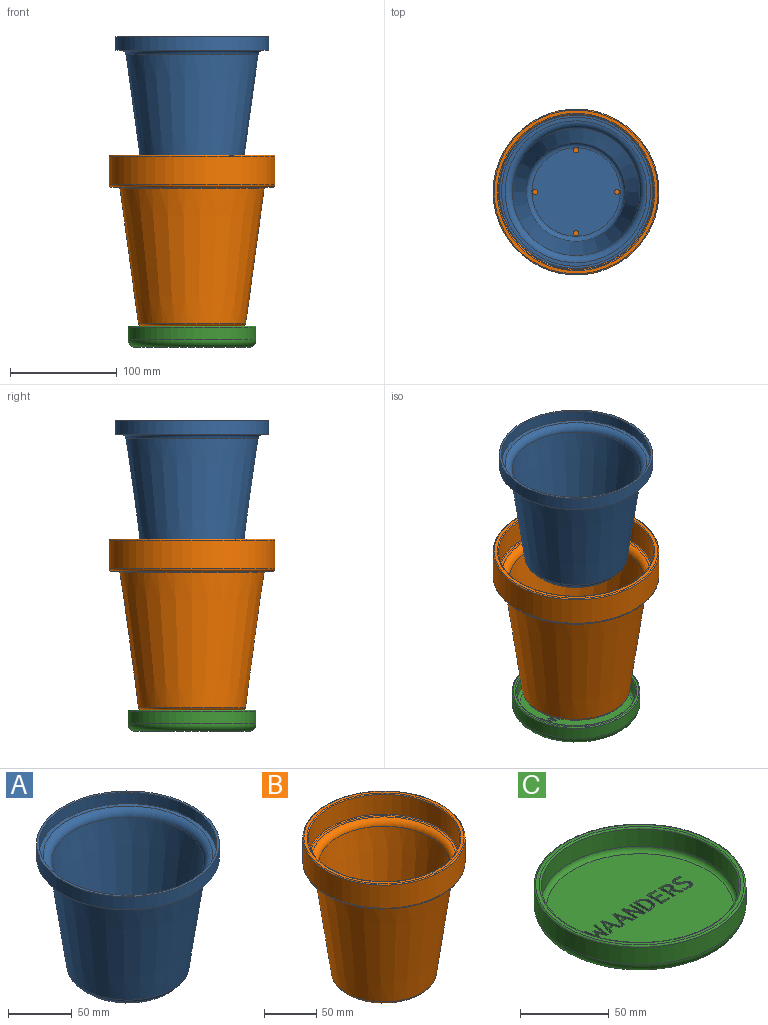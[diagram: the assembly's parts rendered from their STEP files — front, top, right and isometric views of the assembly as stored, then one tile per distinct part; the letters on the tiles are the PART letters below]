
ASSEMBLY  parts=3 mates=2
PART A: 18 faces, bbox 152.3x152.3x122.5 mm
  f0: plane 143.69x143.69mm, normal (0,0,1), area 890.3mm2, adj f1,f11
  f1: cylinder r=69.84mm len=139.69mm, axis (0,0,-1), area 4718.3mm2, adj f0,f2
  f2: cone r=66.5mm half-angle=89.8deg, axis (0,0,1), area 1430.4mm2, adj f1,f3
  f3: torus R=66.8mm, axis (0,0,-1), area 3821.9mm2, adj f2,f4
  f4: cone r=46.37mm half-angle=7.9deg, axis (0,0,1), area 32806.2mm2, adj f3,f5
  f5: torus R=41.42mm, axis (0,0,-1), area 2000.3mm2, adj f4,f6,f12
  f6: plane 82.84x82.84mm, normal (0,0,1), area 5311.8mm2, adj f5,f12,f13,f14,f15
  f7: torus R=43.16mm, axis (0,0,-1), area 2078.9mm2, adj f8,f16
  f8: cone r=48.12mm half-angle=7.9deg, axis (0,0,1), area 34557.6mm2, adj f7,f9
  f9: torus R=66.8mm, axis (0,0,-1), area 2871.9mm2, adj f8,f10
  f10: plane 143.69x143.69mm, normal (0,0,-1), area 2197.8mm2, adj f9,f11
  f11: cylinder r=71.84mm len=143.69mm, axis (0,0,-1), area 5758.6mm2, adj f0,f10
  f12: cylinder r=2.5mm len=5mm, axis (0,0,-1), area 62.8mm2, adj f5,f6,f17
  f13: cylinder r=2.5mm len=5mm, axis (0,0,-1), area 62.8mm2, adj f6,f17
  f14: cylinder r=2.5mm len=5mm, axis (0,0,-1), area 62.8mm2, adj f6,f17
  f15: cylinder r=2.5mm len=5mm, axis (0,0,-1), area 62.8mm2, adj f6,f17
  f16: cylinder r=43.16mm len=86.33mm, axis (0,0,1), area 542.4mm2, adj f7,f17
  f17: plane 86.33x86.33mm, normal (0,0,-1), area 5774.6mm2, adj f12,f13,f14,f15,f16
PART B: 150 faces, bbox 168.2x168.2x160 mm
  f0: plane 94.76x94.76mm, normal (0,0,-1), area 6749.7mm2, adj f15,f21,f22,f23,f24,f25,f26,f27
  f1: torus R=69.47mm, axis (0,0,-1), area 1231.2mm2, adj f2,f16
  f2: plane 151.44x151.44mm, normal (0,0,-1), area 2852.6mm2, adj f1,f3
  f3: torus R=75.72mm, axis (0,0,-1), area 1519.8mm2, adj f2,f4
  f4: cylinder r=77.72mm len=155.44mm, axis (0,0,-1), area 13186.1mm2, adj f3,f5
  f5: torus R=76.72mm, axis (0,0,-1), area 762.4mm2, adj f4,f6
  f6: cone r=76.72mm half-angle=89.9deg, axis (0,0,-1), area 1417.9mm2, adj f5,f7
  f7: torus R=73.72mm, axis (0,0,-1), area 722.4mm2, adj f6,f8
  f8: cylinder r=72.72mm len=145.44mm, axis (0,0,-1), area 10513.3mm2, adj f7,f9
  f9: torus R=71.72mm, axis (0,0,-1), area 714.1mm2, adj f8,f10
  f10: plane 143.44x143.44mm, normal (0,0,1), area 999.8mm2, adj f9,f11
  f11: torus R=69.47mm, axis (0,0,-1), area 4119mm2, adj f10,f12
  f12: cone r=45.99mm half-angle=7.8deg, axis (0,0,1), area 41754.1mm2, adj f11,f13
  f13: torus R=43.02mm, axis (0,0,-1), area 1212.7mm2, adj f12,f14
  f14: plane 86.03x86.03mm, normal (0,0,1), area 5813.3mm2, adj f13
  f15: torus R=47.38mm, axis (0,0,-1), area 1330.8mm2, adj f0,f16
  f16: cone r=50.35mm half-angle=7.8deg, axis (0,0,1), area 46955.4mm2, adj f1,f15
  f17: plane 2.97x2mm, normal (0.95,-0.3,0), area 6.2mm2, adj f18,f29,f30,f146
  f18: plane 2.7x2mm, normal (0,1,0), area 5.4mm2, adj f17,f19,f30,f146
  f19: plane 3.27x2mm, normal (-0.96,-0.29,0), area 6.8mm2, adj f18,f20,f30,f146
  f20: extruded ~2x1.28mm, area 2.6mm2, adj f19,f29,f30,f146
  f21: plane 3.17x2mm, normal (0.95,-0.3,0), area 6.7mm2, adj f0,f22,f28,f30
  f22: plane 2x1.34mm, normal (0,-1,0), area 2.7mm2, adj f0,f21,f23,f30
  f23: plane 10.28x3.4mm, normal (-0.95,0.31,0), area 21.7mm2, adj f0,f22,f24,f30
  f24: plane 2x1.36mm, normal (0,1,0), area 2.7mm2, adj f0,f23,f25,f30
  f25: plane 10.28x3.38mm, normal (0.95,0.31,0), area 21.6mm2, adj f0,f24,f26,f30
  f26: plane 2x1.33mm, normal (0,-1,0), area 2.7mm2, adj f0,f25,f27,f30
  f27: plane 3.17x2mm, normal (-0.95,-0.31,0), area 6.7mm2, adj f0,f26,f28,f30
  f28: plane 3.44x2mm, normal (0,-1,0), area 6.9mm2, adj f0,f21,f27,f30
  f29: extruded ~2x1.58mm, area 3.3mm2, adj f17,f20,f30,f146
  f30: plane 10.28x8.14mm, normal (0,0,-1), area 28.9mm2, adj f17,f18,f19,f20,f21,f22,f23,f24
  f31: plane 2x1.25mm, normal (1,0,0), area 2.5mm2, adj f0,f32,f50,f51
  f32: extruded ~2.9x2mm, area 5.9mm2, adj f0,f31,f33,f51
  f33: extruded ~2.76x2mm, area 5.8mm2, adj f0,f32,f34,f51
  f34: extruded ~2.11x2mm, area 4.8mm2, adj f0,f33,f35,f51
  f35: extruded ~2x1.68mm, area 3.6mm2, adj f0,f34,f36,f51
  f36: extruded ~2.3x2mm, area 5.3mm2, adj f0,f35,f37,f51
  f37: extruded ~2x1.89mm, area 4.2mm2, adj f0,f36,f38,f51
  f38: extruded ~2x1.15mm, area 2.5mm2, adj f0,f37,f39,f51
  f39: extruded ~2.05x2mm, area 5.7mm2, adj f0,f38,f40,f51
  f40: extruded ~2.52x2mm, area 5.2mm2, adj f0,f39,f41,f51
  f41: plane 2x1.15mm, normal (-0.93,-0.36,0), area 2.5mm2, adj f0,f40,f42,f51
  f42: extruded ~2.91x2mm, area 6mm2, adj f0,f41,f43,f51
  f43: extruded ~2.47x2mm, area 5.2mm2, adj f0,f42,f44,f51
  f44: extruded ~2x1.91mm, area 4.4mm2, adj f0,f43,f45,f51
  f45: extruded ~2x1.85mm, area 4mm2, adj f0,f44,f46,f51
  f46: extruded ~2.09x2mm, area 4.9mm2, adj f0,f45,f47,f51
  f47: extruded ~2x2mm, area 4.4mm2, adj f0,f46,f48,f51
  f48: extruded ~2x1.12mm, area 2.5mm2, adj f0,f47,f49,f51
  f49: extruded ~2.45x2mm, area 6.8mm2, adj f0,f48,f50,f51
  f50: extruded ~2.9x2mm, area 6mm2, adj f0,f31,f49,f51
  f51: plane 10.52x6.62mm, normal (0,0,-1), area 26.4mm2, adj f31,f32,f33,f34,f35,f36,f37,f38
  f52: plane 5.89x2mm, normal (0,-1,0), area 11.8mm2, adj f0,f53,f63,f64
  f53: plane 2x1.15mm, normal (-1,0,0), area 2.3mm2, adj f0,f52,f54,f64
  f54: plane 4.59x2mm, normal (0,1,0), area 9.2mm2, adj f0,f53,f55,f64
  f55: plane 3.64x2mm, normal (-1,0,0), area 7.3mm2, adj f0,f54,f56,f64
  f56: plane 4.32x2mm, normal (0,-1,0), area 8.6mm2, adj f0,f55,f57,f64
  f57: plane 2x1.13mm, normal (-1,0,0), area 2.3mm2, adj f0,f56,f58,f64
  f58: plane 4.32x2mm, normal (0,1,0), area 8.6mm2, adj f0,f57,f59,f64
  f59: plane 3.16x2mm, normal (-1,0,0), area 6.3mm2, adj f0,f58,f60,f64
  f60: plane 4.59x2mm, normal (0,-1,0), area 9.2mm2, adj f0,f59,f61,f64
  f61: plane 2x1.15mm, normal (-1,0,0), area 2.3mm2, adj f0,f60,f62,f64
  f62: plane 5.89x2mm, normal (0,1,0), area 11.8mm2, adj f0,f61,f63,f64
  f63: plane 10.24x2mm, normal (1,0,0), area 20.5mm2, adj f0,f52,f62,f64
  f64: plane 10.24x5.89mm, normal (0,0,-1), area 28.8mm2, adj f52,f53,f54,f55,f56,f57,f58,f59
  f65: plane 2x1.51mm, normal (0,-1,0), area 3mm2, adj f0,f66,f78,f79
  f66: plane 10.24x2mm, normal (-1,0,0), area 20.5mm2, adj f0,f65,f67,f79
  f67: plane 2x1.22mm, normal (0,1,0), area 2.4mm2, adj f0,f66,f68,f79
  f68: plane 5.6x2mm, normal (1,0,0), area 11.2mm2, adj f0,f67,f69,f79
  f69: extruded ~2.83x2mm, area 5.7mm2, adj f0,f68,f70,f79
  f70: plane 2x0.04mm, normal (0,1,0), area 0.1mm2, adj f0,f69,f71,f79
  f71: plane 8.43x4.05mm, normal (-0.9,0.43,0), area 18.7mm2, adj f0,f70,f72,f79
  f72: plane 2x1.49mm, normal (0,1,0), area 3mm2, adj f0,f71,f73,f79
  f73: plane 10.24x2mm, normal (1,0,0), area 20.5mm2, adj f0,f72,f74,f79
  f74: plane 2x1.2mm, normal (0,-1,0), area 2.4mm2, adj f0,f73,f75,f79
  f75: plane 5.55x2mm, normal (-1,0,0), area 11.1mm2, adj f0,f74,f76,f79
  f76: extruded ~2.92x2mm, area 5.8mm2, adj f0,f75,f77,f79
  f77: plane 2x0.06mm, normal (0,-1,0), area 0.1mm2, adj f0,f76,f78,f79
  f78: plane 8.47x4.06mm, normal (0.9,-0.43,0), area 18.8mm2, adj f0,f65,f77,f79
  f79: plane 10.24x6.7mm, normal (0,0,-1), area 35.1mm2, adj f65,f66,f67,f68,f69,f70,f71,f72
  f80: plane 2.97x2mm, normal (0.95,-0.3,0), area 6.2mm2, adj f81,f92,f93,f147
  f81: plane 2.7x2mm, normal (0,1,0), area 5.4mm2, adj f80,f82,f93,f147
  f82: plane 3.27x2mm, normal (-0.96,-0.29,0), area 6.8mm2, adj f81,f83,f93,f147
  f83: extruded ~2x1.28mm, area 2.6mm2, adj f82,f92,f93,f147
  f84: plane 3.17x2mm, normal (0.95,-0.3,0), area 6.7mm2, adj f0,f85,f91,f93
  f85: plane 2x1.34mm, normal (0,-1,0), area 2.7mm2, adj f0,f84,f86,f93
  f86: plane 10.28x3.4mm, normal (-0.95,0.31,0), area 21.7mm2, adj f0,f85,f87,f93
  f87: plane 2x1.36mm, normal (0,1,0), area 2.7mm2, adj f0,f86,f88,f93
  f88: plane 10.28x3.38mm, normal (0.95,0.31,0), area 21.6mm2, adj f0,f87,f89,f93
  f89: plane 2x1.33mm, normal (0,-1,0), area 2.7mm2, adj f0,f88,f90,f93
  f90: plane 3.17x2mm, normal (-0.95,-0.31,0), area 6.7mm2, adj f0,f89,f91,f93
  f91: plane 3.44x2mm, normal (0,-1,0), area 6.9mm2, adj f0,f84,f90,f93
  f92: extruded ~2x1.58mm, area 3.3mm2, adj f80,f83,f93,f147
  f93: plane 10.28x8.14mm, normal (0,0,-1), area 28.9mm2, adj f80,f81,f82,f83,f84,f85,f86,f87
  f94: plane 8x2mm, normal (-1,0,0), area 16mm2, adj f95,f105,f106,f148
  f95: plane 2x0.95mm, normal (0,-1,0), area 1.9mm2, adj f94,f96,f106,f148
  f96: extruded ~3.95x3.45mm, area 12mm2, adj f95,f97,f106,f148
  f97: extruded ~4.05x3.73mm, area 12.6mm2, adj f96,f105,f106,f148
  f98: plane 10.24x2mm, normal (1,0,0), area 20.5mm2, adj f0,f99,f104,f106
  f99: plane 2.11x2mm, normal (0,-1,0), area 4.2mm2, adj f0,f98,f100,f106
  f100: extruded ~3.7x2mm, area 8.1mm2, adj f0,f99,f101,f106
  f101: extruded ~3.87x2mm, area 8.4mm2, adj f0,f100,f102,f106
  f102: extruded ~3.7x2mm, area 8mm2, adj f0,f101,f103,f106
  f103: extruded ~3.45x2mm, area 7.6mm2, adj f0,f102,f104,f106
  f104: plane 2.4x2mm, normal (0,1,0), area 4.8mm2, adj f0,f98,f103,f106
  f105: plane 2x0.67mm, normal (0,1,0), area 1.3mm2, adj f94,f97,f106,f148
  f106: plane 10.24x7.08mm, normal (0,0,-1), area 33.3mm2, adj f94,f95,f96,f97,f98,f99,f100,f101
  f107: plane 2x1.15mm, normal (0,1,0), area 2.3mm2, adj f108,f123,f124,f149
  f108: plane 3.79x2mm, normal (-1,0,0), area 7.6mm2, adj f107,f109,f124,f149
  f109: plane 2x1.11mm, normal (0,-1,0), area 2.2mm2, adj f108,f110,f124,f149
  f110: extruded ~2x1.81mm, area 3.8mm2, adj f109,f111,f124,f149
  f111: extruded ~2x1.42mm, area 3.2mm2, adj f110,f112,f124,f149
  f112: extruded ~2x1.47mm, area 3.3mm2, adj f111,f123,f124,f149
  f113: plane 4.23x2mm, normal (-1,0,0), area 8.5mm2, adj f0,f114,f122,f124
  f114: plane 2x1.6mm, normal (0,-1,0), area 3.2mm2, adj f0,f113,f115,f124
  f115: plane 4.23x2.45mm, normal (0.87,-0.5,0), area 9.8mm2, adj f0,f114,f116,f124
  f116: plane 2x1.53mm, normal (0,-1,0), area 3.1mm2, adj f0,f115,f117,f124
  f117: plane 4.59x2.78mm, normal (-0.86,0.52,0), area 10.7mm2, adj f0,f116,f118,f124
  f118: extruded ~2.74x2.02mm, area 7.3mm2, adj f0,f117,f119,f124
  f119: extruded ~3.64x2.91mm, area 10.7mm2, adj f0,f118,f120,f124
  f120: plane 2.5x2mm, normal (0,1,0), area 5mm2, adj f0,f119,f121,f124
  f121: plane 10.24x2mm, normal (1,0,0), area 20.5mm2, adj f0,f120,f122,f124
  f122: plane 2x1.31mm, normal (0,-1,0), area 2.6mm2, adj f0,f113,f121,f124
  f123: extruded ~2x1.77mm, area 3.7mm2, adj f107,f112,f124,f149
  f124: plane 10.24x6.9mm, normal (0,0,-1), area 33mm2, adj f107,f108,f109,f110,f111,f112,f113,f114
  f125: plane 2x1.24mm, normal (0,1,0), area 2.5mm2, adj f0,f126,f144,f145
  f126: plane 3.61x2mm, normal (0.96,0.26,0), area 7.5mm2, adj f0,f125,f127,f145
  f127: extruded ~2.18x2mm, area 4.5mm2, adj f0,f126,f128,f145
  f128: extruded ~2x1.69mm, area 3.4mm2, adj f0,f127,f129,f145
  f129: extruded ~2.65x2mm, area 5.3mm2, adj f0,f128,f130,f145
  f130: plane 4.64x2mm, normal (-0.99,0.13,0), area 9.4mm2, adj f0,f129,f131,f145
  f131: plane 2x1.19mm, normal (0,1,0), area 2.4mm2, adj f0,f130,f132,f145
  f132: plane 10.24x2mm, normal (0.99,-0.14,0), area 20.7mm2, adj f0,f131,f133,f145
  f133: plane 2x1.33mm, normal (0,-1,0), area 2.7mm2, adj f0,f132,f134,f145
  f134: plane 4.05x2mm, normal (-0.97,-0.26,0), area 8.4mm2, adj f0,f133,f135,f145
  f135: extruded ~2x1.99mm, area 4.1mm2, adj f0,f134,f136,f145
  f136: extruded ~2x1.97mm, area 4.1mm2, adj f0,f135,f137,f145
  f137: plane 4.06x2mm, normal (0.96,-0.28,0), area 8.5mm2, adj f0,f136,f138,f145
  f138: plane 2x1.33mm, normal (0,-1,0), area 2.7mm2, adj f0,f137,f139,f145
  f139: plane 10.24x2mm, normal (-0.99,-0.13,0), area 20.6mm2, adj f0,f138,f140,f145
  f140: plane 2x1.19mm, normal (0,1,0), area 2.4mm2, adj f0,f139,f141,f145
  f141: plane 4.64x2mm, normal (0.99,0.11,0), area 9.3mm2, adj f0,f140,f142,f145
  f142: extruded ~4.33x2mm, area 8.7mm2, adj f0,f141,f143,f145
  f143: extruded ~2.15x2mm, area 4.4mm2, adj f0,f142,f144,f145
  f144: plane 3.65x2mm, normal (-0.96,0.27,0), area 7.6mm2, adj f0,f125,f143,f145
  f145: plane 10.24x8.58mm, normal (0,0,-1), area 34.8mm2, adj f125,f126,f127,f128,f129,f130,f131,f132
  f146: plane 4.55x2.7mm, normal (0,0,-1), area 5.9mm2, adj f17,f18,f19,f20,f29
  f147: plane 4.55x2.7mm, normal (0,0,-1), area 5.9mm2, adj f80,f81,f82,f83,f92
  f148: plane 8x4.4mm, normal (0,0,-1), area 30.4mm2, adj f94,f95,f96,f97,f105
  f149: plane 3.79x3.48mm, normal (0,0,-1), area 11.8mm2, adj f107,f108,f109,f110,f111,f112,f123
PART C: 142 faces, bbox 129.6x129.6x20 mm
  f0: plane 105.75x105.75mm, normal (0,0,1), area 8387.7mm2, adj f4,f13,f14,f15,f16,f17,f18,f19
  f1: plane 117.75x117.75mm, normal (0,0,1), area 727.3mm2, adj f2,f8
  f2: torus R=56.88mm, axis (0,0,-1), area 555.1mm2, adj f1,f3
  f3: cylinder r=55.88mm len=111.75mm, axis (0,0,-1), area 4213mm2, adj f2,f4
  f4: torus R=52.88mm, axis (0,0,-1), area 1622.2mm2, adj f0,f3
  f5: plane 105.75x105.75mm, normal (0,0,-1), area 8783.6mm2, adj f6
  f6: torus R=52.88mm, axis (0,0,-1), area 3961mm2, adj f5,f7
  f7: cylinder r=59.88mm len=119.75mm, axis (0,0,-1), area 4514.6mm2, adj f6,f8
  f8: torus R=58.88mm, axis (0,0,-1), area 587.4mm2, adj f1,f7
  f9: plane 3.39x2mm, normal (0.95,0.3,0), area 7.1mm2, adj f10,f21,f22,f138
  f10: plane 3.08x2mm, normal (0,-1,0), area 6.2mm2, adj f9,f11,f22,f138
  f11: plane 3.74x2mm, normal (-0.96,0.29,0), area 7.8mm2, adj f10,f12,f22,f138
  f12: extruded ~2x1.46mm, area 3mm2, adj f11,f21,f22,f138
  f13: plane 3.63x2mm, normal (0.95,0.3,0), area 7.6mm2, adj f0,f14,f20,f22
  f14: plane 2x1.54mm, normal (0,1,0), area 3.1mm2, adj f0,f13,f15,f22
  f15: plane 11.75x3.88mm, normal (-0.95,-0.31,0), area 24.7mm2, adj f0,f14,f16,f22
  f16: plane 2x1.56mm, normal (0,-1,0), area 3.1mm2, adj f0,f15,f17,f22
  f17: plane 11.75x3.87mm, normal (0.95,-0.31,0), area 24.7mm2, adj f0,f16,f18,f22
  f18: plane 2x1.52mm, normal (0,1,0), area 3mm2, adj f0,f17,f19,f22
  f19: plane 3.63x2mm, normal (-0.95,0.31,0), area 7.6mm2, adj f0,f18,f20,f22
  f20: plane 3.93x2mm, normal (0,1,0), area 7.9mm2, adj f0,f13,f19,f22
  f21: extruded ~2x1.81mm, area 3.8mm2, adj f9,f12,f22,f138
  f22: plane 11.75x9.31mm, normal (0,0,1), area 37.7mm2, adj f9,f10,f11,f12,f13,f14,f15,f16
  f23: plane 2x1.42mm, normal (1,0,0), area 2.8mm2, adj f0,f24,f42,f43
  f24: extruded ~3.31x2mm, area 6.8mm2, adj f0,f23,f25,f43
  f25: extruded ~3.15x2mm, area 6.7mm2, adj f0,f24,f26,f43
  f26: extruded ~2.41x2mm, area 5.5mm2, adj f0,f25,f27,f43
  f27: extruded ~2x1.92mm, area 4.2mm2, adj f0,f26,f28,f43
  f28: extruded ~2.63x2mm, area 6.1mm2, adj f0,f27,f29,f43
  f29: extruded ~2.17x2mm, area 4.9mm2, adj f0,f28,f30,f43
  f30: extruded ~2x1.31mm, area 2.9mm2, adj f0,f29,f31,f43
  f31: extruded ~2.34x2mm, area 6.6mm2, adj f0,f30,f32,f43
  f32: extruded ~2.88x2mm, area 5.9mm2, adj f0,f31,f33,f43
  f33: plane 2x1.31mm, normal (-0.93,0.36,0), area 2.8mm2, adj f0,f32,f34,f43
  f34: extruded ~3.33x2mm, area 6.8mm2, adj f0,f33,f35,f43
  f35: extruded ~2.82x2mm, area 6mm2, adj f0,f34,f36,f43
  f36: extruded ~2.18x2mm, area 5mm2, adj f0,f35,f37,f43
  f37: extruded ~2.11x2mm, area 4.6mm2, adj f0,f36,f38,f43
  f38: extruded ~2.39x2mm, area 5.6mm2, adj f0,f37,f39,f43
  f39: extruded ~2.28x2mm, area 5.1mm2, adj f0,f38,f40,f43
  f40: extruded ~2x1.28mm, area 2.9mm2, adj f0,f39,f41,f43
  f41: extruded ~2.8x2mm, area 7.7mm2, adj f0,f40,f42,f43
  f42: extruded ~3.31x2mm, area 6.8mm2, adj f0,f23,f41,f43
  f43: plane 12.03x7.57mm, normal (0,0,1), area 34.5mm2, adj f23,f24,f25,f26,f27,f28,f29,f30
  f44: plane 6.74x2mm, normal (0,1,0), area 13.5mm2, adj f0,f45,f55,f56
  f45: plane 2x1.31mm, normal (-1,0,0), area 2.6mm2, adj f0,f44,f46,f56
  f46: plane 5.25x2mm, normal (0,-1,0), area 10.5mm2, adj f0,f45,f47,f56
  f47: plane 4.16x2mm, normal (-1,0,0), area 8.3mm2, adj f0,f46,f48,f56
  f48: plane 4.94x2mm, normal (0,1,0), area 9.9mm2, adj f0,f47,f49,f56
  f49: plane 2x1.3mm, normal (-1,0,0), area 2.6mm2, adj f0,f48,f50,f56
  f50: plane 4.94x2mm, normal (0,-1,0), area 9.9mm2, adj f0,f49,f51,f56
  f51: plane 3.62x2mm, normal (-1,0,0), area 7.2mm2, adj f0,f50,f52,f56
  f52: plane 5.25x2mm, normal (0,1,0), area 10.5mm2, adj f0,f51,f53,f56
  f53: plane 2x1.31mm, normal (-1,0,0), area 2.6mm2, adj f0,f52,f54,f56
  f54: plane 6.74x2mm, normal (0,-1,0), area 13.5mm2, adj f0,f53,f55,f56
  f55: plane 11.7x2mm, normal (1,0,0), area 23.4mm2, adj f0,f44,f54,f56
  f56: plane 11.7x6.74mm, normal (0,0,1), area 37.6mm2, adj f44,f45,f46,f47,f48,f49,f50,f51
  f57: plane 2x1.72mm, normal (0,1,0), area 3.4mm2, adj f0,f58,f70,f71
  f58: plane 11.7x2mm, normal (-1,0,0), area 23.4mm2, adj f0,f57,f59,f71
  f59: plane 2x1.39mm, normal (0,-1,0), area 2.8mm2, adj f0,f58,f60,f71
  f60: plane 6.4x2mm, normal (1,0,0), area 12.8mm2, adj f0,f59,f61,f71
  f61: extruded ~3.23x2mm, area 6.5mm2, adj f0,f60,f62,f71
  f62: plane 2x0.05mm, normal (0,-1,0), area 0.1mm2, adj f0,f61,f63,f71
  f63: plane 9.64x4.62mm, normal (-0.9,-0.43,0), area 21.4mm2, adj f0,f62,f64,f71
  f64: plane 2x1.71mm, normal (0,-1,0), area 3.4mm2, adj f0,f63,f65,f71
  f65: plane 11.7x2mm, normal (1,0,0), area 23.4mm2, adj f0,f64,f66,f71
  f66: plane 2x1.38mm, normal (0,1,0), area 2.7mm2, adj f0,f65,f67,f71
  f67: plane 6.35x2mm, normal (-1,0,0), area 12.7mm2, adj f0,f66,f68,f71
  f68: extruded ~3.34x2mm, area 6.7mm2, adj f0,f67,f69,f71
  f69: plane 2x0.06mm, normal (0,1,0), area 0.1mm2, adj f0,f68,f70,f71
  f70: plane 9.68x4.64mm, normal (0.9,0.43,0), area 21.5mm2, adj f0,f57,f69,f71
  f71: plane 11.7x7.66mm, normal (0,0,1), area 45.9mm2, adj f57,f58,f59,f60,f61,f62,f63,f64
  f72: plane 3.39x2mm, normal (0.95,0.3,0), area 7.1mm2, adj f73,f84,f85,f139
  f73: plane 3.08x2mm, normal (0,-1,0), area 6.2mm2, adj f72,f74,f85,f139
  f74: plane 3.74x2mm, normal (-0.96,0.29,0), area 7.8mm2, adj f73,f75,f85,f139
  f75: extruded ~2x1.46mm, area 3mm2, adj f74,f84,f85,f139
  f76: plane 3.63x2mm, normal (0.95,0.3,0), area 7.6mm2, adj f0,f77,f83,f85
  f77: plane 2x1.54mm, normal (0,1,0), area 3.1mm2, adj f0,f76,f78,f85
  f78: plane 11.75x3.88mm, normal (-0.95,-0.31,0), area 24.7mm2, adj f0,f77,f79,f85
  f79: plane 2x1.56mm, normal (0,-1,0), area 3.1mm2, adj f0,f78,f80,f85
  f80: plane 11.75x3.87mm, normal (0.95,-0.31,0), area 24.7mm2, adj f0,f79,f81,f85
  f81: plane 2x1.52mm, normal (0,1,0), area 3mm2, adj f0,f80,f82,f85
  f82: plane 3.63x2mm, normal (-0.95,0.31,0), area 7.6mm2, adj f0,f81,f83,f85
  f83: plane 3.93x2mm, normal (0,1,0), area 7.9mm2, adj f0,f76,f82,f85
  f84: extruded ~2x1.81mm, area 3.8mm2, adj f72,f75,f85,f139
  f85: plane 11.75x9.31mm, normal (0,0,1), area 37.7mm2, adj f72,f73,f74,f75,f76,f77,f78,f79
  f86: plane 9.15x2mm, normal (-1,0,0), area 18.3mm2, adj f87,f97,f98,f140
  f87: plane 2x1.08mm, normal (0,1,0), area 2.2mm2, adj f86,f88,f98,f140
  f88: extruded ~4.51x3.95mm, area 13.7mm2, adj f87,f89,f98,f140
  f89: extruded ~4.63x4.26mm, area 14.4mm2, adj f88,f97,f98,f140
  f90: plane 11.7x2mm, normal (1,0,0), area 23.4mm2, adj f0,f91,f96,f98
  f91: plane 2.41x2mm, normal (0,1,0), area 4.8mm2, adj f0,f90,f92,f98
  f92: extruded ~4.22x2mm, area 9.2mm2, adj f0,f91,f93,f98
  f93: extruded ~4.42x2mm, area 9.6mm2, adj f0,f92,f94,f98
  f94: extruded ~4.23x2mm, area 9.1mm2, adj f0,f93,f95,f98
  f95: extruded ~3.95x2mm, area 8.7mm2, adj f0,f94,f96,f98
  f96: plane 2.74x2mm, normal (0,-1,0), area 5.5mm2, adj f0,f90,f95,f98
  f97: plane 2x0.77mm, normal (0,-1,0), area 1.5mm2, adj f86,f89,f98,f140
  f98: plane 11.7x8.1mm, normal (0,0,1), area 43.5mm2, adj f86,f87,f88,f89,f90,f91,f92,f93
  f99: plane 2x1.31mm, normal (0,-1,0), area 2.6mm2, adj f100,f115,f116,f141
  f100: plane 4.33x2mm, normal (-1,0,0), area 8.7mm2, adj f99,f101,f116,f141
  f101: plane 2x1.27mm, normal (0,1,0), area 2.5mm2, adj f100,f102,f116,f141
  f102: extruded ~2.06x2mm, area 4.3mm2, adj f101,f103,f116,f141
  f103: extruded ~2x1.62mm, area 3.6mm2, adj f102,f104,f116,f141
  f104: extruded ~2x1.68mm, area 3.7mm2, adj f103,f115,f116,f141
  f105: plane 4.83x2mm, normal (-1,0,0), area 9.7mm2, adj f0,f106,f114,f116
  f106: plane 2x1.83mm, normal (0,1,0), area 3.7mm2, adj f0,f105,f107,f116
  f107: plane 4.83x2.8mm, normal (0.87,0.5,0), area 11.2mm2, adj f0,f106,f108,f116
  f108: plane 2x1.75mm, normal (0,1,0), area 3.5mm2, adj f0,f107,f109,f116
  f109: plane 5.24x3.18mm, normal (-0.86,-0.52,0), area 12.3mm2, adj f0,f108,f110,f116
  f110: extruded ~3.14x2.31mm, area 8.4mm2, adj f0,f109,f111,f116
  f111: extruded ~4.16x3.32mm, area 12.2mm2, adj f0,f110,f112,f116
  f112: plane 2.86x2mm, normal (0,-1,0), area 5.7mm2, adj f0,f111,f113,f116
  f113: plane 11.7x2mm, normal (1,0,0), area 23.4mm2, adj f0,f112,f114,f116
  f114: plane 2x1.5mm, normal (0,1,0), area 3mm2, adj f0,f105,f113,f116
  f115: extruded ~2.02x2mm, area 4.3mm2, adj f99,f104,f116,f141
  f116: plane 11.7x7.88mm, normal (0,0,1), area 43.1mm2, adj f99,f100,f101,f102,f103,f104,f105,f106
  f117: plane 2x1.42mm, normal (0,-1,0), area 2.8mm2, adj f0,f118,f136,f137
  f118: plane 4.13x2mm, normal (0.96,-0.26,0), area 8.6mm2, adj f0,f117,f119,f137
  f119: extruded ~2.5x2mm, area 5.1mm2, adj f0,f118,f120,f137
  f120: extruded ~2x1.93mm, area 3.9mm2, adj f0,f119,f121,f137
  f121: extruded ~3.03x2mm, area 6.1mm2, adj f0,f120,f122,f137
  f122: plane 5.31x2mm, normal (-0.99,-0.13,0), area 10.7mm2, adj f0,f121,f123,f137
  f123: plane 2x1.36mm, normal (0,-1,0), area 2.7mm2, adj f0,f122,f124,f137
  f124: plane 11.7x2mm, normal (0.99,0.14,0), area 23.6mm2, adj f0,f123,f125,f137
  f125: plane 2x1.52mm, normal (0,1,0), area 3mm2, adj f0,f124,f126,f137
  f126: plane 4.62x2mm, normal (-0.97,0.26,0), area 9.6mm2, adj f0,f125,f127,f137
  f127: extruded ~2.27x2mm, area 4.7mm2, adj f0,f126,f128,f137
  f128: extruded ~2.26x2mm, area 4.6mm2, adj f0,f127,f129,f137
  f129: plane 4.64x2mm, normal (0.96,0.28,0), area 9.7mm2, adj f0,f128,f130,f137
  f130: plane 2x1.52mm, normal (0,1,0), area 3mm2, adj f0,f129,f131,f137
  f131: plane 11.7x2mm, normal (-0.99,0.13,0), area 23.6mm2, adj f0,f130,f132,f137
  f132: plane 2x1.36mm, normal (0,-1,0), area 2.7mm2, adj f0,f131,f133,f137
  f133: plane 5.31x2mm, normal (0.99,-0.11,0), area 10.7mm2, adj f0,f132,f134,f137
  f134: extruded ~4.95x2mm, area 10mm2, adj f0,f133,f135,f137
  f135: extruded ~2.46x2mm, area 5mm2, adj f0,f134,f136,f137
  f136: plane 4.17x2mm, normal (-0.96,-0.27,0), area 8.7mm2, adj f0,f117,f135,f137
  f137: plane 11.7x9.8mm, normal (0,0,1), area 45.4mm2, adj f117,f118,f119,f120,f121,f122,f123,f124
  f138: plane 5.2x3.08mm, normal (0,0,1), area 7.7mm2, adj f9,f10,f11,f12,f21
  f139: plane 5.2x3.08mm, normal (0,0,1), area 7.7mm2, adj f72,f73,f74,f75,f84
  f140: plane 9.15x5.03mm, normal (0,0,1), area 39.7mm2, adj f86,f87,f88,f89,f97
  f141: plane 4.33x3.98mm, normal (0,0,1), area 15.4mm2, adj f99,f100,f101,f102,f103,f104,f115
PLACE A t=(-36.76,-2.18,99.2)mm
PLACE B t=(-36.76,-2.18,-23.42)mm fixed
PLACE C t=(-36.76,-2.18,-37.29)mm
MATE slider B.f1 <-> A.f1  axis (0,0,-1) through (-36.76,-2.18,94.06)mm
MATE slider B.f1 <-> C.f2  axis (0,0,1) through (-36.76,-2.18,13.99)mm
